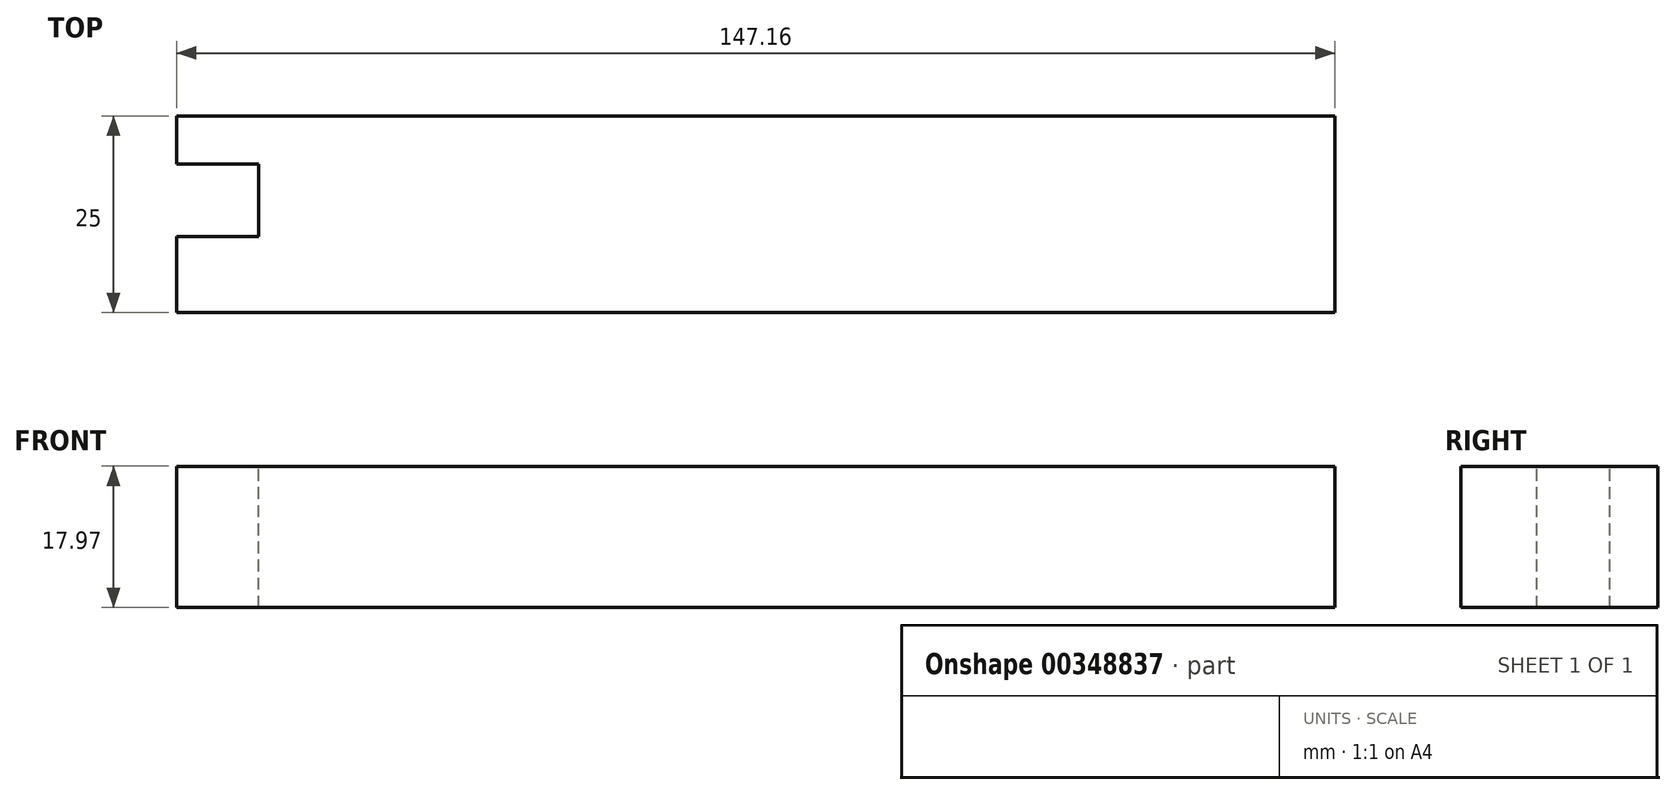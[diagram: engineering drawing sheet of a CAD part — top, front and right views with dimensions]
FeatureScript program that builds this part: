
annotation { "Feature Type Name" : "Feature", "Feature Type Description" : "" }
export const myFeature = defineFeature(function(context is Context, id is Id, definition is map)
    precondition{}
    {
        {
            var Q0;
            Q0=qCreatedBy(makeId("Front.planeOp"),FACE);
            var sketch = newSketch(context, id + "F0", { "sketchPlane" : qUnion([Q0])});
            skLineSegment(sketch, "E0.bottom", {"start": v(-124.35, 29.4) * mm, "end": v(22.8, 29.4) * mm});
            skLineSegment(sketch, "E0.top", {"start": v(-124.35, 11.44) * mm, "end": v(22.8, 11.44) * mm});
            skLineSegment(sketch, "E0.left", {"start": v(-124.35, 29.4) * mm, "end": v(-124.35, 11.44) * mm});
            skLineSegment(sketch, "E0.right", {"start": v(22.8, 29.4) * mm, "end": v(22.8, 11.44) * mm});
            skSolve(sketch);
        }
        {
            var Q0;
            Q0 = qSketchRegion(id + "F0", true);
            extrude(context, id + "F1", {"entities" : qUnion([Q0]), "depth" : 25 * mm});
        }
        {
            var Q0;
            Q0=makeQuery(id+"F1.opExtrude","SWEPT_FACE",FACE,{"disambiguationData":[OSD([sQuery(id+"F0.wireOp",EDGE,"E0.bottom")])]});
            var sketch = newSketch(context, id + "F2", { "sketchPlane" : qUnion([Q0])});
            skLineSegment(sketch, "E1", {"start": v(-124.35, -15.34) * mm, "end": v(-113.94, -15.34) * mm});
            skLineSegment(sketch, "E2", {"start": v(-113.94, -15.34) * mm, "end": v(-113.94, -6.1) * mm});
            skLineSegment(sketch, "E3", {"start": v(-113.94, -6.1) * mm, "end": v(-124.35, -6.1) * mm});
            skSolve(sketch);
        }
        {
            var Q0;
            {var subQ0=sQuery(id+"F2.wireOp",EDGE,"E1");Q0=makeQuery(id+"F2.imprint","IMPRINT",FACE,{"disambiguationData":[TD([[makeQuery(id+"F2.imprint","IMPRINT",EDGE,{"derivedFrom":subQ0}),1.0]])]});}
            var sketch = newSketch(context, id + "F3", { "sketchPlane" : qUnion([Q0])});
            skSolve(sketch);
        }
        {
            var Q0;
            Q0 = qSketchRegion(id + "F3", true);
            var Q1;
            {var subQ0=sQuery(id+"F2.wireOp",EDGE,"E1");Q1=makeQuery(id+"F2.imprint","IMPRINT",FACE,{"disambiguationData":[TD([[makeQuery(id+"F2.imprint","IMPRINT",EDGE,{"derivedFrom":subQ0}),1.0]])]});}
            extrude(context, id + "F4", {"entities" : qUnion([Q0, Q1]), "operationType" : NewBodyOperationType.REMOVE, "endBound" : BoundingType.THROUGH_ALL, "oppositeDirection" : true, "depth" : 25 * mm});
        }
    });
